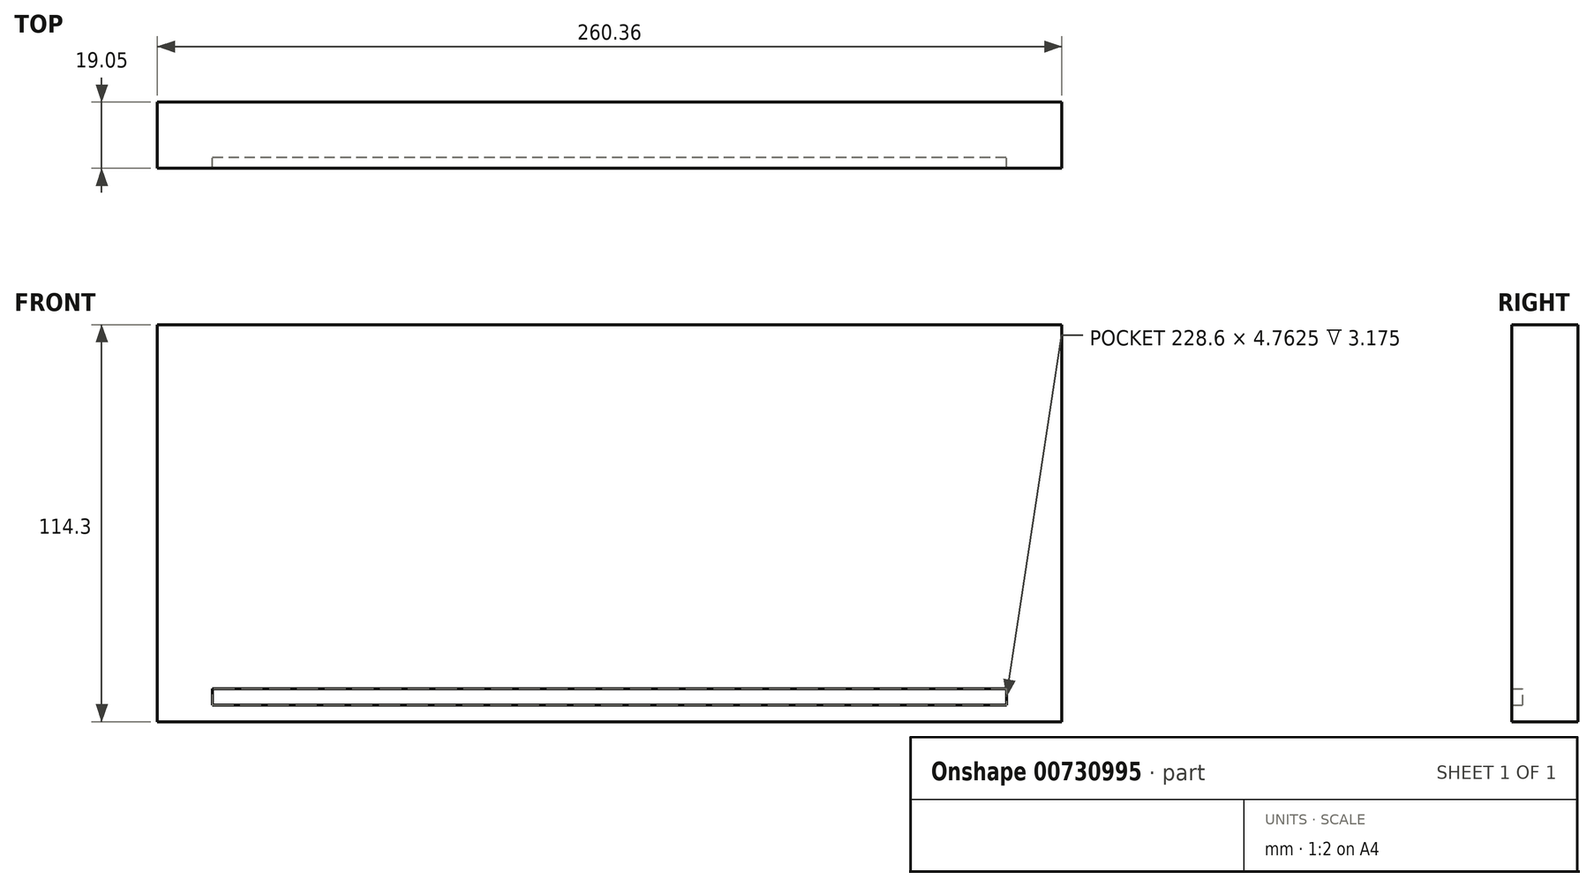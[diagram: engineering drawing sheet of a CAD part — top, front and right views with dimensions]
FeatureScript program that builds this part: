
annotation { "Feature Type Name" : "Feature", "Feature Type Description" : "" }
export const myFeature = defineFeature(function(context is Context, id is Id, definition is map)
    precondition{}
    {
        {
            var Q0;
            Q0=qCreatedBy(makeId("Front.planeOp"),FACE);
            var sketch = newSketch(context, id + "F0", { "sketchPlane" : qUnion([Q0])});
            skLineSegment(sketch, "E0.bottom", {"start": v(130.18, -57.15) * mm, "end": v(-130.17, -57.15) * mm});
            skLineSegment(sketch, "E0.top", {"start": v(130.18, 57.15) * mm, "end": v(-130.18, 57.15) * mm});
            skLineSegment(sketch, "E0.left", {"start": v(130.18, -57.15) * mm, "end": v(130.18, 57.15) * mm});
            skLineSegment(sketch, "E0.right", {"start": v(-130.18, -57.15) * mm, "end": v(-130.18, 57.15) * mm});
            skPoint(sketch, "E0.middle", {"position": v(0, 0) * mm});
            skSolve(sketch);
        }
        {
            var Q0;
            Q0=makeQuery(id+"F0.imprint","IMPRINT",FACE,{"disambiguationData":[TD([[makeQuery(id+"F0.imprint","IMPRINT",EDGE,{"derivedFrom":sQuery(id+"F0.wireOp",EDGE,"E0.bottom")}),-1.0]])]});
            extrude(context, id + "F1", {"entities" : qUnion([Q0]), "depth" : 19.05 * mm, "offsetDistance" : 25.4 * mm});
        }
        {
            var Q0;
            Q0=makeQuery(id+"F1.opExtrude","CAP_FACE",FACE,{"disambiguationData":[OSD([sQuery(id+"F0.wireOp",EDGE,"E0.bottom"),sQuery(id+"F0.wireOp",EDGE,"E0.top"),sQuery(id+"F0.wireOp",EDGE,"E0.left"),sQuery(id+"F0.wireOp",EDGE,"E0.right")])],"isStart":false});
            var sketch = newSketch(context, id + "F2", { "sketchPlane" : qUnion([Q0])});
            skLineSegment(sketch, "E1.bottom", {"start": v(-130.18, -47.62) * mm, "end": v(130.18, -47.62) * mm});
            skLineSegment(sketch, "E1.top", {"start": v(-130.17, -52.39) * mm, "end": v(130.18, -52.39) * mm});
            skLineSegment(sketch, "E1.left", {"start": v(-130.18, -47.62) * mm, "end": v(-130.18, -52.39) * mm});
            skLineSegment(sketch, "E1.right", {"start": v(130.18, -47.62) * mm, "end": v(130.18, -52.39) * mm});
            skSolve(sketch);
        }
        {
            var Q0;
            Q0=makeQuery(id+"F2.imprint","IMPRINT",FACE,{"disambiguationData":[TD([[makeQuery(id+"F2.imprint","IMPRINT",EDGE,{"derivedFrom":sQuery(id+"F2.wireOp",EDGE,"E1.bottom")}),-1.0]])]});
            extrude(context, id + "F3", {"entities" : qUnion([Q0]), "operationType" : NewBodyOperationType.REMOVE, "oppositeDirection" : true, "depth" : 3.17 * mm, "offsetDistance" : 25.4 * mm});
        }
        {
            var Q0;
            Q0=makeQuery(id+"F3.boolean.opBoolean","COPY",FACE,{"derivedFrom":makeQuery(id+"F3.opExtrude","CAP_FACE",FACE,{"disambiguationData":[OSD([sQuery(id+"F2.wireOp",EDGE,"E1.bottom"),sQuery(id+"F2.wireOp",EDGE,"E1.top"),sQuery(id+"F2.wireOp",EDGE,"E1.left"),sQuery(id+"F2.wireOp",EDGE,"E1.right")])],"isStart":false})});
            var sketch = newSketch(context, id + "F4", { "sketchPlane" : qUnion([Q0])});
            skLineSegment(sketch, "E2.bottom", {"start": v(-130.18, -47.62) * mm, "end": v(-114.3, -47.62) * mm});
            skLineSegment(sketch, "E2.top", {"start": v(-130.18, -52.39) * mm, "end": v(-114.3, -52.39) * mm});
            skLineSegment(sketch, "E2.left", {"start": v(-130.18, -47.62) * mm, "end": v(-130.18, -52.39) * mm});
            skLineSegment(sketch, "E2.right", {"start": v(-114.3, -47.62) * mm, "end": v(-114.3, -52.39) * mm});
            skLineSegment(sketch, "E3.bottom", {"start": v(130.18, -52.39) * mm, "end": v(114.3, -52.39) * mm});
            skLineSegment(sketch, "E3.top", {"start": v(130.18, -47.62) * mm, "end": v(114.3, -47.62) * mm});
            skLineSegment(sketch, "E3.left", {"start": v(130.18, -52.39) * mm, "end": v(130.18, -47.62) * mm});
            skLineSegment(sketch, "E3.right", {"start": v(114.3, -52.39) * mm, "end": v(114.3, -47.62) * mm});
            skSolve(sketch);
        }
        {
            var Q0;
            Q0=makeQuery(id+"F4.imprint","IMPRINT",FACE,{"disambiguationData":[TD([[makeQuery(id+"F4.imprint","IMPRINT",EDGE,{"derivedFrom":sQuery(id+"F4.wireOp",EDGE,"E3.bottom")}),1.0]])]});
            var Q1;
            Q1=makeQuery(id+"F4.imprint","IMPRINT",FACE,{"disambiguationData":[TD([[makeQuery(id+"F4.imprint","IMPRINT",EDGE,{"derivedFrom":sQuery(id+"F4.wireOp",EDGE,"E2.bottom")}),-1.0]])]});
            extrude(context, id + "F5", {"entities" : qUnion([Q0, Q1]), "operationType" : NewBodyOperationType.ADD, "depth" : 3.17 * mm, "offsetDistance" : 25.4 * mm});
        }
    });
